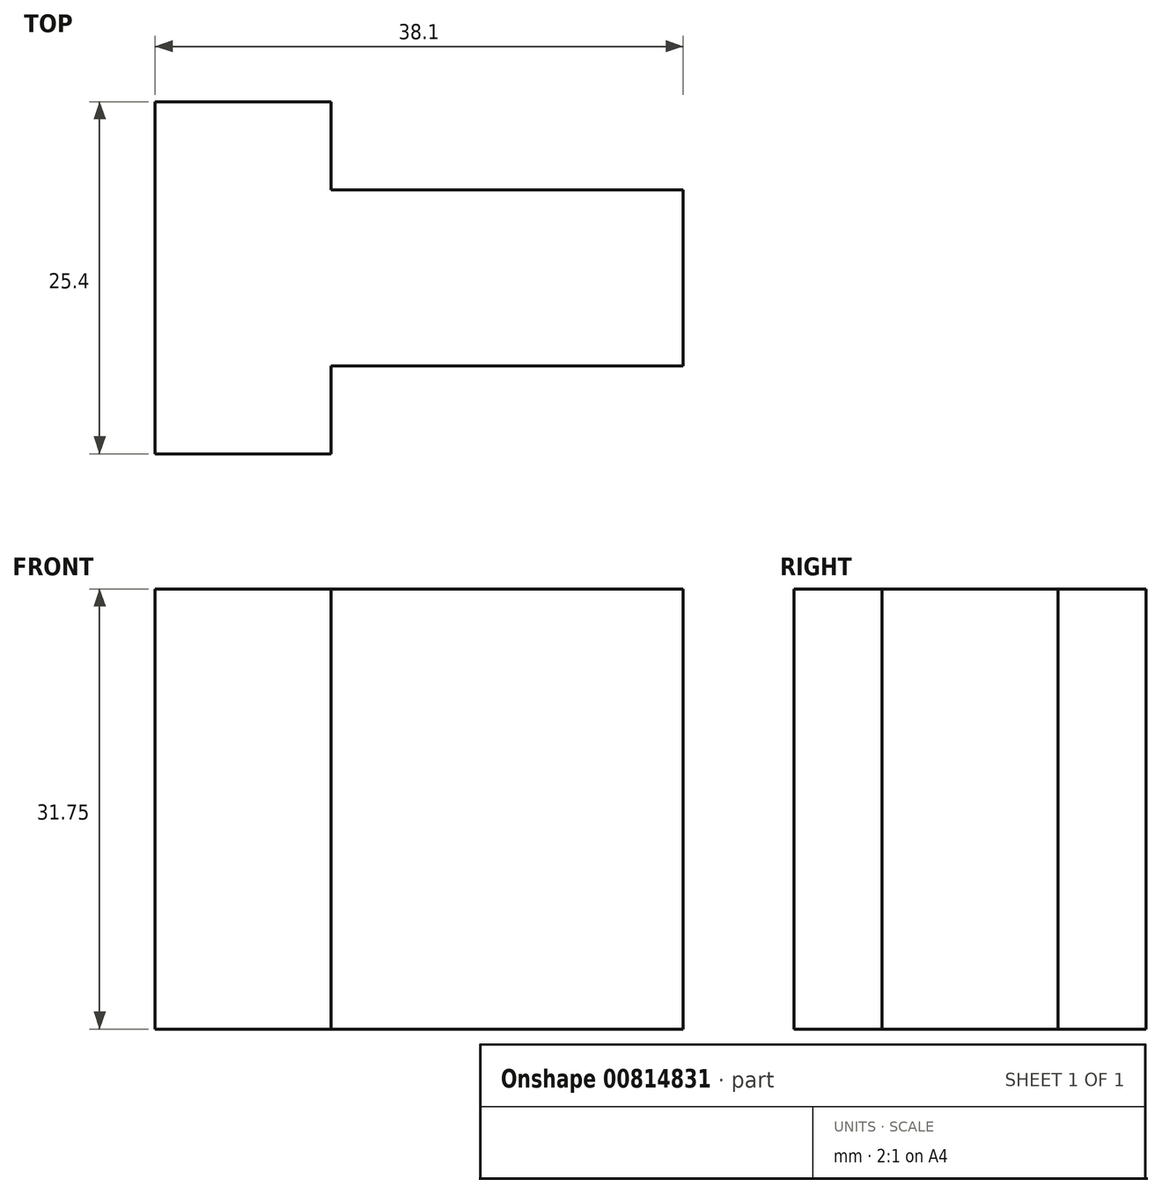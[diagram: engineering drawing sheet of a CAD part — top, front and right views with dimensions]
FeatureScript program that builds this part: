
annotation { "Feature Type Name" : "Feature", "Feature Type Description" : "" }
export const myFeature = defineFeature(function(context is Context, id is Id, definition is map)
    precondition{}
    {
        {
            var Q0;
            Q0=qCreatedBy(makeId("Top.planeOp"),FACE);
            var sketch = newSketch(context, id + "F0", { "sketchPlane" : qUnion([Q0])});
            skLineSegment(sketch, "E0", {"start": v(0, 0) * mm, "end": v(-25.4, 0) * mm});
            skLineSegment(sketch, "E1", {"start": v(-25.4, 0) * mm, "end": v(-25.4, -6.35) * mm});
            skLineSegment(sketch, "E2", {"start": v(-25.4, -6.35) * mm, "end": v(-38.1, -6.35) * mm});
            skLineSegment(sketch, "E3", {"start": v(-38.1, -6.35) * mm, "end": v(-38.1, 19.05) * mm});
            skLineSegment(sketch, "E4", {"start": v(-38.1, 19.05) * mm, "end": v(-25.4, 19.05) * mm});
            skLineSegment(sketch, "E5", {"start": v(-25.4, 19.05) * mm, "end": v(-25.4, 12.7) * mm});
            skLineSegment(sketch, "E6", {"start": v(-25.4, 12.7) * mm, "end": v(0, 12.7) * mm});
            skLineSegment(sketch, "E7", {"start": v(0, 12.7) * mm, "end": v(0, 0) * mm});
            skSolve(sketch);
        }
        {
            var Q0;
            Q0=makeQuery(id+"F0.imprint","IMPRINT",FACE,{"disambiguationData":[TD([[makeQuery(id+"F0.imprint","IMPRINT",EDGE,{"derivedFrom":sQuery(id+"F0.wireOp",EDGE,"E0")}),-1.0]])]});
            extrude(context, id + "F1", {"entities" : qUnion([Q0]), "depth" : 31.75 * mm, "offsetDistance" : 25.4 * mm});
        }
    });
